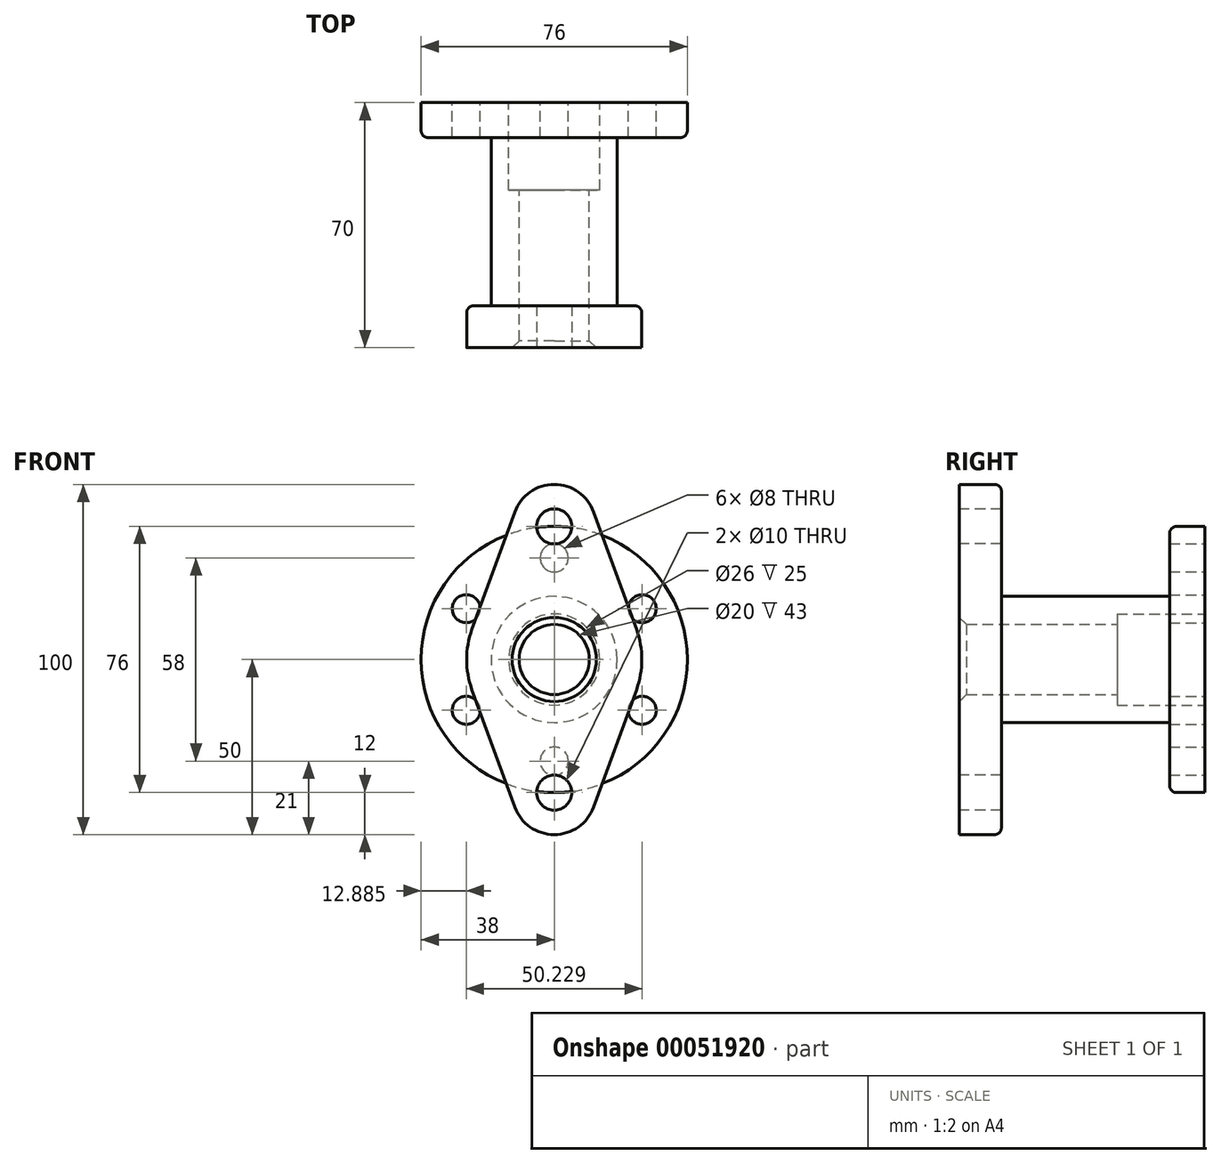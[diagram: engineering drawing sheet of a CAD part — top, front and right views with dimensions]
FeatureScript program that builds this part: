
annotation { "Feature Type Name" : "Feature", "Feature Type Description" : "" }
export const myFeature = defineFeature(function(context is Context, id is Id, definition is map)
    precondition{}
    {
        {
            var Q0;
            Q0=qCreatedBy(makeId("Front.planeOp"),FACE);
            var sketch = newSketch(context, id + "F0", { "sketchPlane" : qUnion([Q0])});
            skCircle(sketch, "E0", {"center": v(0, 0) * mm, "radius": 38 * mm});
            skCircle(sketch, "E1", {"center": v(0, 29) * mm, "radius": 4 * mm});
            skCircle(sketch, "E2.1.0", {"center": v(-25.11, 14.5) * mm, "radius": 4 * mm});
            skCircle(sketch, "E2.2.0", {"center": v(-25.11, -14.5) * mm, "radius": 4 * mm});
            skCircle(sketch, "E2.3.0", {"center": v(0, -29) * mm, "radius": 4 * mm});
            skCircle(sketch, "E2.4.0", {"center": v(25.11, -14.5) * mm, "radius": 4 * mm});
            skCircle(sketch, "E2.5.0", {"center": v(25.11, 14.5) * mm, "radius": 4 * mm});
            skSolve(sketch);
        }
        {
            var Q0;
            Q0=makeQuery(id+"F0.imprint","IMPRINT",FACE,{"disambiguationData":[TD([[makeQuery(id+"F0.imprint","IMPRINT",EDGE,{"derivedFrom":sQuery(id+"F0.wireOp",EDGE,"E0")}),1.0]])]});
            extrude(context, id + "F1", {"entities" : qUnion([Q0]), "depth" : 10 * mm});
        }
        {
            var Q0;
            Q0=qCreatedBy(makeId("Front.planeOp"),FACE);
            cPlane(context, id + "F2", {"entities" : qUnion([Q0]), "cplaneType" : CPlaneType.OFFSET, "offset" : 70 * mm, "width" : 150 * mm, "height" : 150 * mm});
        }
        {
            var Q0;
            Q0=qCreatedBy(id+"F2.planeOp",FACE);
            var sketch = newSketch(context, id + "F3", { "sketchPlane" : qUnion([Q0])});
            skArc(sketch, "E3", {"start": v(23.5, -8.55) * mm, "mid": v(25, 0) * mm, "end": v(23.5, 8.55) * mm});
            skArc(sketch, "E4", {"start": v(-11.28, -42.1) * mm, "mid": v(0, -50) * mm, "end": v(11.28, -42.1) * mm});
            skArc(sketch, "E5.MirrorC", {"start": v(-11.28, 42.1) * mm, "mid": v(0, 50) * mm, "end": v(11.28, 42.1) * mm});
            skLineSegment(sketch, "E6", {"start": v(-11.28, -42.1) * mm, "end": v(-23.5, -8.55) * mm});
            skLineSegment(sketch, "E7", {"start": v(11.28, -42.1) * mm, "end": v(23.5, -8.55) * mm});
            skLineSegment(sketch, "E8.MirrorCS", {"start": v(-11.28, 42.1) * mm, "end": v(-23.5, 8.55) * mm});
            skLineSegment(sketch, "E9.MirrorCS", {"start": v(11.28, 42.1) * mm, "end": v(23.5, 8.55) * mm});
            skArc(sketch, "E10.trimOffspring", {"start": v(-23.5, 8.55) * mm, "mid": v(-25, 0) * mm, "end": v(-23.5, -8.55) * mm});
            skCircle(sketch, "E11", {"center": v(0, 38) * mm, "radius": 5 * mm});
            skCircle(sketch, "E12", {"center": v(0, -38) * mm, "radius": 5 * mm});
            skSolve(sketch);
        }
        {
            var Q0;
            Q0=makeQuery(id+"F3.imprint","IMPRINT",FACE,{"disambiguationData":[TD([[makeQuery(id+"F3.imprint","IMPRINT",EDGE,{"derivedFrom":sQuery(id+"F3.wireOp",EDGE,"E3")}),1.0]])]});
            var Q1;
            Q1=makeQuery(id+"F1.opExtrude","CAP_FACE",FACE,{"disambiguationData":[OSD([sQuery(id+"F0.wireOp",EDGE,"E0"),sQuery(id+"F0.wireOp",EDGE,"E1"),sQuery(id+"F0.wireOp",EDGE,"E2.1.0"),sQuery(id+"F0.wireOp",EDGE,"E2.2.0"),sQuery(id+"F0.wireOp",EDGE,"E2.3.0"),sQuery(id+"F0.wireOp",EDGE,"E2.4.0"),sQuery(id+"F0.wireOp",EDGE,"E2.5.0")])],"isStart":false});
            var Q2;
            Q2=makeQuery(id+"F1.opExtrude","CAP_FACE",FACE,{"disambiguationData":[OSD([sQuery(id+"F0.wireOp",EDGE,"E0"),sQuery(id+"F0.wireOp",EDGE,"E1"),sQuery(id+"F0.wireOp",EDGE,"E2.1.0"),sQuery(id+"F0.wireOp",EDGE,"E2.2.0"),sQuery(id+"F0.wireOp",EDGE,"E2.3.0"),sQuery(id+"F0.wireOp",EDGE,"E2.4.0"),sQuery(id+"F0.wireOp",EDGE,"E2.5.0")])],"isStart":true});
            extrude(context, id + "F4", {"entities" : qUnion([Q0, Q1, Q2]), "operationType" : NewBodyOperationType.ADD, "oppositeDirection" : true, "depth" : 12 * mm});
        }
        {
            var Q0;
            Q0=makeQuery(id+"F1.opExtrude","CAP_FACE",FACE,{"disambiguationData":[OSD([sQuery(id+"F0.wireOp",EDGE,"E0"),sQuery(id+"F0.wireOp",EDGE,"E1"),sQuery(id+"F0.wireOp",EDGE,"E2.1.0"),sQuery(id+"F0.wireOp",EDGE,"E2.2.0"),sQuery(id+"F0.wireOp",EDGE,"E2.3.0"),sQuery(id+"F0.wireOp",EDGE,"E2.4.0"),sQuery(id+"F0.wireOp",EDGE,"E2.5.0")])],"isStart":false});
            var sketch = newSketch(context, id + "F5", { "sketchPlane" : qUnion([Q0])});
            skCircle(sketch, "E13", {"center": v(0, 0) * mm, "radius": 18 * mm});
            skSolve(sketch);
        }
        {
            var Q0;
            Q0 = qSketchRegion(id + "F5", true);
            extrude(context, id + "F6", {"entities" : qUnion([Q0]), "operationType" : NewBodyOperationType.ADD, "endBound" : BoundingType.UP_TO_NEXT, "depth" : 25 * mm});
        }
        {
            var Q0;
            Q0=qCreatedBy(makeId("Right.planeOp"),FACE);
            var sketch = newSketch(context, id + "F7", { "sketchPlane" : qUnion([Q0])});
            skLineSegment(sketch, "E14.bottom", {"start": v(18.92, 43.87) * mm, "end": v(0, 43.87) * mm});
            skLineSegment(sketch, "E14.top", {"start": v(18.92, -41.82) * mm, "end": v(0, -41.82) * mm});
            skLineSegment(sketch, "E14.left", {"start": v(18.92, 43.87) * mm, "end": v(18.92, -41.82) * mm});
            skLineSegment(sketch, "E14.right", {"start": v(0, 43.87) * mm, "end": v(0, -41.82) * mm});
            skSolve(sketch);
        }
        {
            var Q0;
            Q0 = qSketchRegion(id + "F7", true);
            extrude(context, id + "F8", {"entities" : qUnion([Q0]), "operationType" : NewBodyOperationType.REMOVE, "endBound" : BoundingType.SYMMETRIC, "oppositeDirection" : true, "depth" : 80 * mm});
        }
        {
            var Q0;
            Q0=makeQuery(id+"F8.boolean.opBoolean","COPY",FACE,{"derivedFrom":makeQuery(id+"F8.opExtrude","SWEPT_FACE",FACE,{"disambiguationData":[OSD([sQuery(id+"F7.wireOp",EDGE,"E14.right")])]})});
            var sketch = newSketch(context, id + "F9", { "sketchPlane" : qUnion([Q0])});
            skCircle(sketch, "E15", {"center": v(0, 0) * mm, "radius": 13 * mm});
            skSolve(sketch);
        }
        {
            var Q0;
            Q0=makeQuery(id+"F9.imprint","IMPRINT",FACE,{"disambiguationData":[TD([[makeQuery(id+"F9.imprint","IMPRINT",EDGE,{"derivedFrom":sQuery(id+"F9.wireOp",EDGE,"E15")}),1.0]])]});
            extrude(context, id + "F10", {"entities" : qUnion([Q0]), "operationType" : NewBodyOperationType.REMOVE, "oppositeDirection" : true, "depth" : 25 * mm});
        }
        {
            var Q0;
            Q0=makeQuery(id+"F10.boolean.opBoolean","COPY",FACE,{"derivedFrom":makeQuery(id+"F10.opExtrude","CAP_FACE",FACE,{"disambiguationData":[OSD([sQuery(id+"F9.wireOp",EDGE,"E15")])],"isStart":false})});
            var sketch = newSketch(context, id + "F11", { "sketchPlane" : qUnion([Q0])});
            skCircle(sketch, "E16", {"center": v(0, 0) * mm, "radius": 10 * mm});
            skSolve(sketch);
        }
        {
            var Q0;
            Q0 = qSketchRegion(id + "F11", true);
            extrude(context, id + "F12", {"entities" : qUnion([Q0]), "operationType" : NewBodyOperationType.REMOVE, "endBound" : BoundingType.THROUGH_ALL, "oppositeDirection" : true, "depth" : 25 * mm});
        }
        {
            var Q0;
            Q0=makeQuery(id+"F6.opExtrude","CAP_EDGE",EDGE,{"disambiguationData":[OSD([sQuery(id+"F5.wireOp",EDGE,"E13")])],"isStart":false});
            var Q1;
            Q1=makeQuery(id+"F4.opExtrude","CAP_EDGE",EDGE,{"disambiguationData":[OSD([sQuery(id+"F3.wireOp",EDGE,"E9.MirrorCS")])],"isStart":false});
            var Q2;
            Q2=makeQuery(id+"F6.opExtrude","CAP_EDGE",EDGE,{"disambiguationData":[OSD([sQuery(id+"F5.wireOp",EDGE,"E13")])],"isStart":true});
            var Q3;
            Q3=makeQuery(id+"F1.opExtrude","CAP_EDGE",EDGE,{"disambiguationData":[OSD([sQuery(id+"F0.wireOp",EDGE,"E0")])],"isStart":false});
            fillet(context, id + "F13", {"entities" : qUnion([Q0, Q1, Q2, Q3]), "radius" : 2 * mm, "tangentPropagation" : true, "allowEdgeOverflow" : false});
        }
        {
            var Q0;
            Q0=makeQuery(id+"F12.boolean.opBoolean","INTERSECT",EDGE,{"derivedFrom":[makeQuery(id+"F4.opExtrude","CAP_FACE",FACE,{"disambiguationData":[OSD([sQuery(id+"F3.wireOp",EDGE,"E3"),sQuery(id+"F3.wireOp",EDGE,"E4"),sQuery(id+"F3.wireOp",EDGE,"E5.MirrorC"),sQuery(id+"F3.wireOp",EDGE,"E6"),sQuery(id+"F3.wireOp",EDGE,"E7"),sQuery(id+"F3.wireOp",EDGE,"E8.MirrorCS"),sQuery(id+"F3.wireOp",EDGE,"E9.MirrorCS"),sQuery(id+"F3.wireOp",EDGE,"E10.trimOffspring"),sQuery(id+"F3.wireOp",EDGE,"E11"),sQuery(id+"F3.wireOp",EDGE,"E12")])],"isStart":true}),makeQuery(id+"F12.opExtrude","SWEPT_FACE",FACE,{"disambiguationData":[OSD([sQuery(id+"F11.wireOp",EDGE,"E16")])]})]});
            chamfer(context, id + "F14", {"entities" : qUnion([Q0]), "width" : 2 * mm, "tangentPropagation" : true});
        }
    });
